# Revit family: Kitchen_Taps-Mixers_hansgrohe_14816000-Ecos-Single-lever-kitchen-mixer_
name_source: partatom
category: Plumbing Fixtures
revit_build: Autodesk Revit 2015 (Build: 20140903_1530(x64)
units: mm (PartAtom-declared; Revit-internal decimal feet)

## types (1)
- Chrome 000
    BIMobject category = Taps & Mixers
    BIMobject category code = kitchen-taps
    BIMobject main category = Kitchen
    BIMobject main category code = kitchen
    Brand url = http://www.hansgrohe-int.com
    Default Elevation = 4' - 0"
    Design country = Germany
    Edition number = 1
    GTIN code = https://4011097686950
    IFC Classification = Sanitary Terminal
    Manufacturer country = Germany
    Manufacturer name = hansgrohe
    Material main = Chrome
    Product Guid = de27fa69-feed-4e65-a44b-5a7131eebf04
    Product SKU = 14816000
    Product data url = https://bimobject.com
    Product family = Ecos
    Product group = Kitchen mixers
    Product name = 14816000 Ecos Single lever kitchen mixer L, 1jet
    QR code = http://bimobject.com

## geometry (parser evidence)
native form markers: Sweep x2
no freeform markers — native parametric forms only
